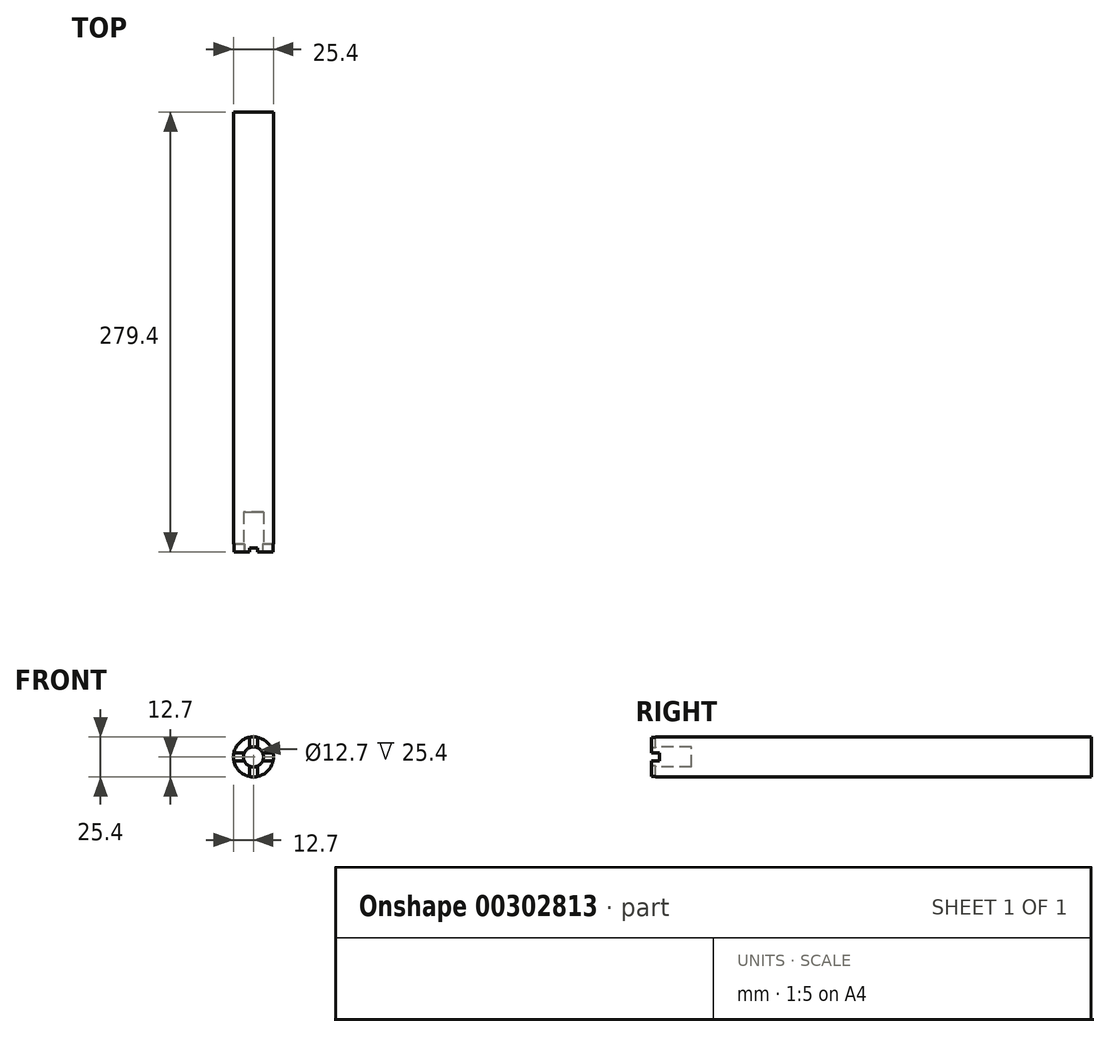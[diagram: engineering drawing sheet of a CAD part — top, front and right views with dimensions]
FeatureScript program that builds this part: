
annotation { "Feature Type Name" : "Feature", "Feature Type Description" : "" }
export const myFeature = defineFeature(function(context is Context, id is Id, definition is map)
    precondition{}
    {
        {
            var Q0;
            Q0=qCreatedBy(makeId("Front.planeOp"),FACE);
            var sketch = newSketch(context, id + "F0", { "sketchPlane" : qUnion([Q0])});
            skCircle(sketch, "E0", {"center": v(0, 0) * mm, "radius": 12.7 * mm});
            skSolve(sketch);
        }
        {
            var Q0;
            Q0 = qSketchRegion(id + "F0", true);
            extrude(context, id + "F1", {"entities" : qUnion([Q0]), "endBound" : BoundingType.SYMMETRIC, "depth" : 279.4 * mm});
        }
        {
            var Q0;
            Q0=makeQuery(id+"F1.opExtrude","CAP_FACE",FACE,{"disambiguationData":[OSD([sQuery(id+"F0.wireOp",EDGE,"E0")])],"isStart":false});
            var sketch = newSketch(context, id + "F2", { "sketchPlane" : qUnion([Q0])});
            skCircle(sketch, "E1", {"center": v(0, 0) * mm, "radius": 6.35 * mm});
            skSolve(sketch);
        }
        {
            var Q0;
            Q0 = qSketchRegion(id + "F2", true);
            extrude(context, id + "F3", {"entities" : qUnion([Q0]), "operationType" : NewBodyOperationType.REMOVE, "oppositeDirection" : true, "depth" : 25.4 * mm});
        }
        {
            var Q0;
            Q0=makeQuery(id+"F1.opExtrude","CAP_FACE",FACE,{"disambiguationData":[OSD([sQuery(id+"F0.wireOp",EDGE,"E0")])],"isStart":false});
            var sketch = newSketch(context, id + "F4", { "sketchPlane" : qUnion([Q0])});
            skLineSegment(sketch, "E2", {"start": v(-2.53, 12.45) * mm, "end": v(-2.53, -12.45) * mm});
            skLineSegment(sketch, "E3", {"start": v(2.55, -12.44) * mm, "end": v(2.55, 12.45) * mm});
            skLineSegment(sketch, "E4", {"start": v(2.55, -16.87) * mm, "end": v(-2.53, -16.87) * mm});
            skLineSegment(sketch, "E5", {"start": v(-2.53, -16.87) * mm, "end": v(-2.53, -12.45) * mm});
            skLineSegment(sketch, "E6", {"start": v(2.55, -12.44) * mm, "end": v(2.55, -16.87) * mm});
            skLineSegment(sketch, "E7", {"start": v(2.55, 12.45) * mm, "end": v(2.55, 18.03) * mm});
            skLineSegment(sketch, "E8", {"start": v(-2.53, 12.45) * mm, "end": v(-2.53, 18.03) * mm});
            skLineSegment(sketch, "E9", {"start": v(-2.53, 18.03) * mm, "end": v(2.55, 18.03) * mm});
            skSolve(sketch);
        }
        {
            var Q0;
            Q0 = qSketchRegion(id + "F4", true);
            extrude(context, id + "F5", {"entities" : qUnion([Q0]), "operationType" : NewBodyOperationType.REMOVE, "oppositeDirection" : true, "depth" : 2.54 * mm});
        }
        {
            var Q0;
            {var subQ0=sQuery(id+"F0.wireOp",EDGE,"E0");Q0=makeQuery(id+"F5.boolean.opBoolean","SPLIT",FACE,{"disambiguationData":[TD([makeQuery(id+"F5.opExtrude","SWEPT_FACE",FACE,{"disambiguationData":[OSD([sQuery(id+"F4.wireOp",EDGE,"E2"),sQuery(id+"F4.wireOp",EDGE,"E5"),sQuery(id+"F4.wireOp",EDGE,"E8")])]})])],"derivedFrom":makeQuery(id+"F1.opExtrude","CAP_FACE",FACE,{"disambiguationData":[OSD([subQ0])],"isStart":false})});}
            var sketch = newSketch(context, id + "F6", { "sketchPlane" : qUnion([Q0])});
            skLineSegment(sketch, "E10", {"start": v(0, 0) * mm, "end": v(25.37, 0) * mm});
            skLineSegment(sketch, "E11", {"start": v(25.37, 0) * mm, "end": v(25.37, 2.7) * mm});
            skLineSegment(sketch, "E12", {"start": v(25.37, 2.7) * mm, "end": v(-15.44, 2.7) * mm});
            skLineSegment(sketch, "E13", {"start": v(-15.44, 2.7) * mm, "end": v(-15.44, -2.38) * mm});
            skLineSegment(sketch, "E14", {"start": v(-15.44, -2.38) * mm, "end": v(25.37, -2.38) * mm});
            skLineSegment(sketch, "E15", {"start": v(25.37, -2.38) * mm, "end": v(25.37, 2.7) * mm});
            skSolve(sketch);
        }
        {
            var Q0;
            Q0 = qSketchRegion(id + "F6", true);
            extrude(context, id + "F7", {"entities" : qUnion([Q0]), "operationType" : NewBodyOperationType.REMOVE, "oppositeDirection" : true, "depth" : 5.08 * mm});
        }
    });
